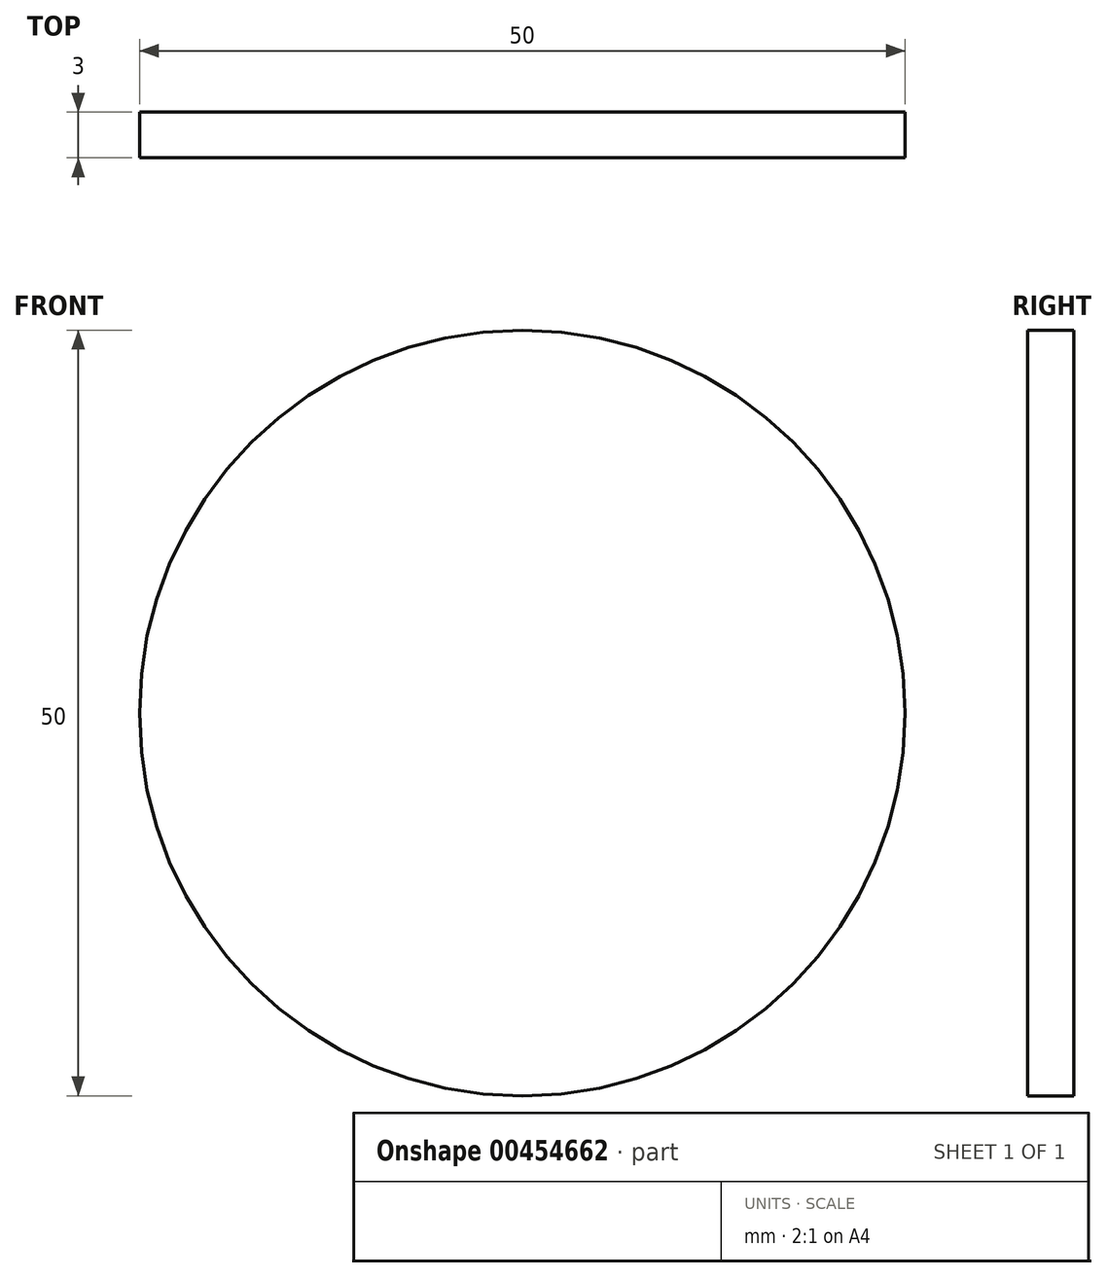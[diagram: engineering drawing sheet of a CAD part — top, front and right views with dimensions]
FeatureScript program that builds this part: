
annotation { "Feature Type Name" : "Feature", "Feature Type Description" : "" }
export const myFeature = defineFeature(function(context is Context, id is Id, definition is map)
    precondition{}
    {
        {
            var Q0;
            Q0=qCreatedBy(makeId("Front.planeOp"),FACE);
            var sketch = newSketch(context, id + "F0", { "sketchPlane" : qUnion([Q0])});
            skCircle(sketch, "E0", {"center": v(0, 0) * mm, "radius": 25 * mm});
            skSolve(sketch);
        }
        {
            var Q0;
            Q0 = qSketchRegion(id + "F0", true);
            extrude(context, id + "F1", {"entities" : qUnion([Q0]), "depth" : 3 * mm});
        }
    });
